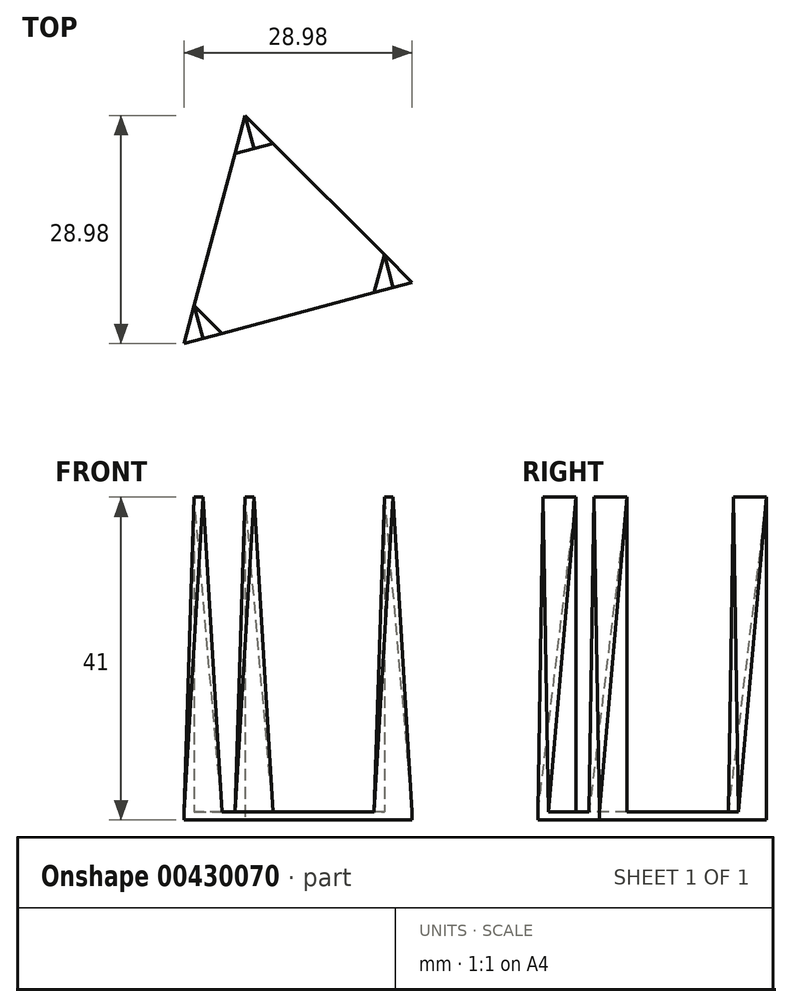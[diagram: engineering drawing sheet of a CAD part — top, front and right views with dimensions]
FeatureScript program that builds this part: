
annotation { "Feature Type Name" : "Feature", "Feature Type Description" : "" }
export const myFeature = defineFeature(function(context is Context, id is Id, definition is map)
    precondition{}
    {
        {
            var Q0;
            Q0=qCreatedBy(makeId("Top.planeOp"),FACE);
            var sketch = newSketch(context, id + "F0", { "sketchPlane" : qUnion([Q0])});
            skLineSegment(sketch, "E0", {"start": v(-4.93, -4.77) * mm, "end": v(2.83, 24.21) * mm});
            skLineSegment(sketch, "E1", {"start": v(2.83, 24.21) * mm, "end": v(24.05, 3) * mm});
            skLineSegment(sketch, "E2", {"start": v(24.05, 3) * mm, "end": v(-4.93, -4.77) * mm});
            skSolve(sketch);
        }
        {
            var Q0;
            Q0 = qSketchRegion(id + "F0", true);
            extrude(context, id + "F1", {"entities" : qUnion([Q0]), "depth" : 1 * mm});
        }
        {
            var Q0;
            Q0=makeQuery(id+"F1.opExtrude","CAP_FACE",FACE,{"disambiguationData":[OSD([sQuery(id+"F0.wireOp",EDGE,"E0"),sQuery(id+"F0.wireOp",EDGE,"E1"),sQuery(id+"F0.wireOp",EDGE,"E2")])],"isStart":false});
            var sketch = newSketch(context, id + "F2", { "sketchPlane" : qUnion([Q0])});
            skLineSegment(sketch, "E3", {"start": v(-4.93, -4.77) * mm, "end": v(-3.64, 0.06) * mm});
            skLineSegment(sketch, "E4", {"start": v(-4.93, -4.77) * mm, "end": v(-0.1, -3.47) * mm});
            skLineSegment(sketch, "E5", {"start": v(-0.1, -3.47) * mm, "end": v(-3.64, 0.06) * mm});
            skLineSegment(sketch, "E6", {"start": v(2.83, 24.21) * mm, "end": v(1.54, 19.38) * mm});
            skLineSegment(sketch, "E7", {"start": v(24.05, 3) * mm, "end": v(19.22, 1.7) * mm});
            skLineSegment(sketch, "E8", {"start": v(2.83, 24.21) * mm, "end": v(6.37, 20.67) * mm});
            skLineSegment(sketch, "E9", {"start": v(24.05, 3) * mm, "end": v(20.5, 6.53) * mm});
            skLineSegment(sketch, "E10", {"start": v(20.5, 6.53) * mm, "end": v(19.22, 1.7) * mm});
            skLineSegment(sketch, "E11", {"start": v(6.37, 20.67) * mm, "end": v(1.54, 19.38) * mm});
            skSolve(sketch);
        }
        {
            var Q0;
            Q0 = qSketchRegion(id + "F2", true);
            extrude(context, id + "F3", {"entities" : qUnion([Q0]), "operationType" : NewBodyOperationType.ADD, "depth" : 40 * mm});
        }
        {
            var Q0;
            Q0=makeQuery(id+"F3.boolean.opBoolean","MERGE",FACE,{"derivedFrom":[makeQuery(id+"F1.opExtrude","SWEPT_FACE",FACE,{"disambiguationData":[OSD([sQuery(id+"F0.wireOp",EDGE,"E2")])]}),makeQuery(id+"F3.opExtrude","SWEPT_FACE",FACE,{"disambiguationData":[OSD([sQuery(id+"F2.wireOp",EDGE,"E4")])]}),makeQuery(id+"F3.opExtrude","SWEPT_FACE",FACE,{"disambiguationData":[OSD([sQuery(id+"F2.wireOp",EDGE,"E7")])]})]});
            var sketch = newSketch(context, id + "F4", { "sketchPlane" : qUnion([Q0])});
            skLineSegment(sketch, "E12", {"start": v(-6, 1) * mm, "end": v(-3.5, 41) * mm});
            skLineSegment(sketch, "E13", {"start": v(-3.5, 41) * mm, "end": v(-1, 1) * mm});
            skLineSegment(sketch, "E14", {"start": v(-1, 1) * mm, "end": v(-1, 41) * mm});
            skLineSegment(sketch, "E15", {"start": v(-1, 41) * mm, "end": v(-6, 41) * mm});
            skLineSegment(sketch, "E16", {"start": v(-6, 41) * mm, "end": v(-6, 1) * mm});
            skLineSegment(sketch, "E17", {"start": v(19, 1) * mm, "end": v(21.5, 41) * mm});
            skLineSegment(sketch, "E18", {"start": v(21.5, 41) * mm, "end": v(24, 1) * mm});
            skLineSegment(sketch, "E19", {"start": v(24, 1) * mm, "end": v(24, 41) * mm});
            skLineSegment(sketch, "E20", {"start": v(24, 41) * mm, "end": v(19, 41) * mm});
            skLineSegment(sketch, "E21", {"start": v(19, 41) * mm, "end": v(19, 1) * mm});
            skSolve(sketch);
        }
        {
            var Q0;
            {var subQ0=sQuery(id+"F4.wireOp",EDGE,"E12");Q0=makeQuery(id+"F4.imprint","IMPRINT",FACE,{"disambiguationData":[TD([[makeQuery(id+"F4.imprint","IMPRINT",EDGE,{"derivedFrom":subQ0}),1.0]])]});}
            var Q1;
            {var subQ0=sQuery(id+"F4.wireOp",EDGE,"E18");Q1=makeQuery(id+"F4.imprint","IMPRINT",FACE,{"disambiguationData":[TD([[makeQuery(id+"F4.imprint","IMPRINT",EDGE,{"derivedFrom":subQ0}),1.0]])]});}
            var Q2;
            {var subQ0=sQuery(id+"F4.wireOp",EDGE,"E13");Q2=makeQuery(id+"F4.imprint","IMPRINT",FACE,{"disambiguationData":[TD([[makeQuery(id+"F4.imprint","IMPRINT",EDGE,{"derivedFrom":subQ0}),1.0]])]});}
            var Q3;
            {var subQ0=sQuery(id+"F4.wireOp",EDGE,"E17");Q3=makeQuery(id+"F4.imprint","IMPRINT",FACE,{"disambiguationData":[TD([[makeQuery(id+"F4.imprint","IMPRINT",EDGE,{"derivedFrom":subQ0}),1.0]])]});}
            extrude(context, id + "F5", {"entities" : qUnion([Q0, Q1, Q2, Q3]), "operationType" : NewBodyOperationType.REMOVE, "endBound" : BoundingType.UP_TO_NEXT, "oppositeDirection" : true, "depth" : 25 * mm});
        }
        {
            var Q0;
            Q0=makeQuery(id+"F3.opExtrude","SWEPT_FACE",FACE,{"disambiguationData":[OSD([sQuery(id+"F2.wireOp",EDGE,"E11")])]});
            var sketch = newSketch(context, id + "F6", { "sketchPlane" : qUnion([Q0])});
            skLineSegment(sketch, "E22", {"start": v(6.5, 1) * mm, "end": v(9, 41) * mm});
            skLineSegment(sketch, "E23", {"start": v(9, 41) * mm, "end": v(6.5, 41) * mm});
            skLineSegment(sketch, "E24", {"start": v(6.5, 41) * mm, "end": v(6.5, 1) * mm});
            skLineSegment(sketch, "E25", {"start": v(9, 41) * mm, "end": v(11.5, 1) * mm});
            skLineSegment(sketch, "E26", {"start": v(11.5, 1) * mm, "end": v(11.5, 41) * mm});
            skLineSegment(sketch, "E27", {"start": v(11.5, 41) * mm, "end": v(9, 41) * mm});
            skSolve(sketch);
        }
        {
            var Q0;
            Q0 = qSketchRegion(id + "F6", true);
            extrude(context, id + "F7", {"entities" : qUnion([Q0]), "operationType" : NewBodyOperationType.REMOVE, "oppositeDirection" : true, "depth" : 25 * mm});
        }
    });
